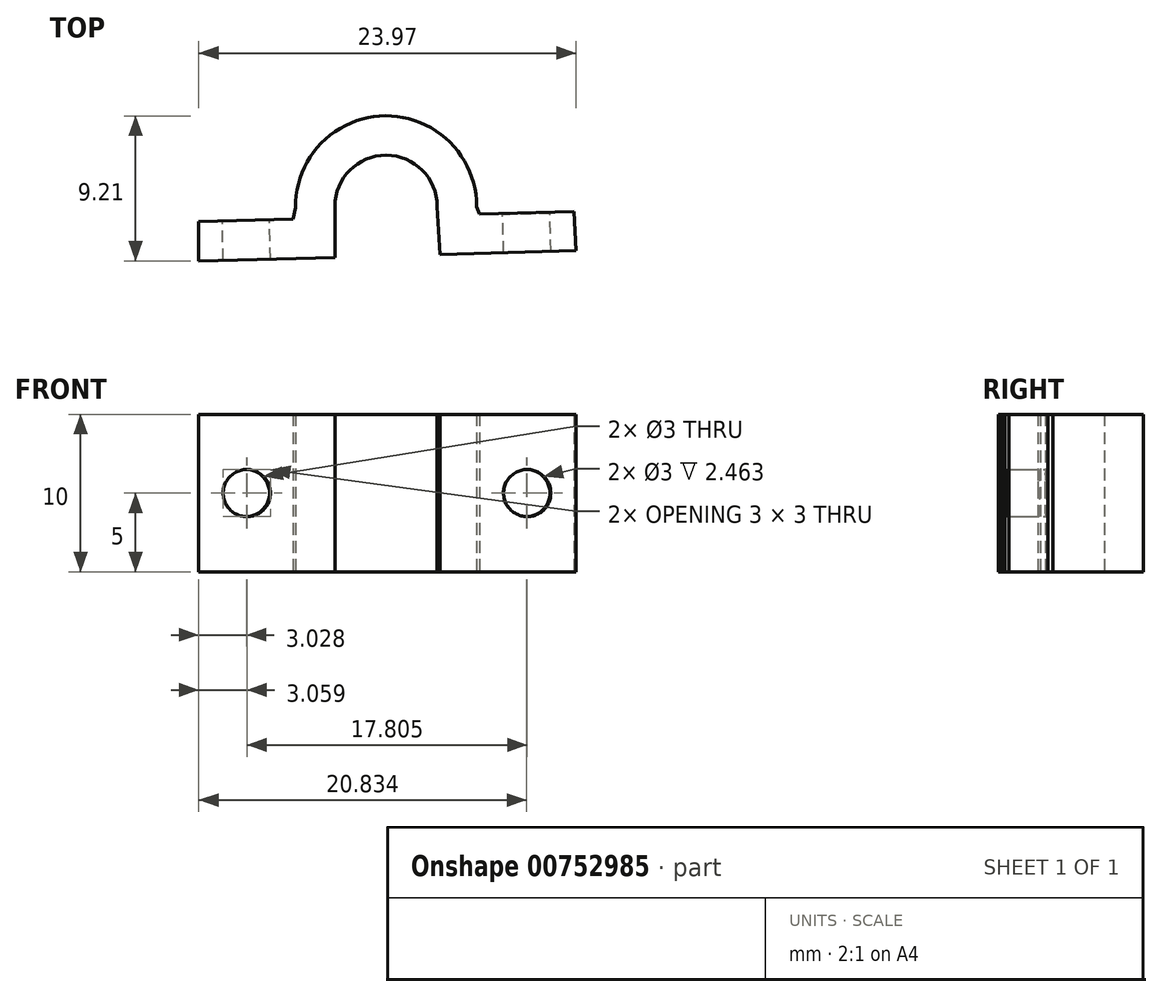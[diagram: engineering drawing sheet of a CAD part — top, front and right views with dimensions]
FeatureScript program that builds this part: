
annotation { "Feature Type Name" : "Feature", "Feature Type Description" : "" }
export const myFeature = defineFeature(function(context is Context, id is Id, definition is map)
    precondition{}
    {
        {
            var Q0;
            Q0=qCreatedBy(makeId("Top.planeOp"),FACE);
            var sketch = newSketch(context, id + "F0", { "sketchPlane" : qUnion([Q0])});
            skArc(sketch, "E0", {"start": v(3.25, 0) * mm, "mid": v(0, 3.25) * mm, "end": v(-3.25, 0) * mm});
            skPoint(sketch, "E1.orphan", {"position": v(0, -3.25) * mm});
            skLineSegment(sketch, "E2", {"start": v(-3.25, -3.25) * mm, "end": v(-11.9, -3.46) * mm});
            skLineSegment(sketch, "E3", {"start": v(-11.9, -3.46) * mm, "end": v(-11.9, -0.96) * mm});
            skLineSegment(sketch, "E4", {"start": v(-11.9, -0.96) * mm, "end": v(-5.9, -0.82) * mm});
            skLineSegment(sketch, "E5", {"start": v(0, 0) * mm, "end": v(-0.36, 13.25) * mm, "construction": true});
            skPoint(sketch, "E5.endSnap0", {"position": v(-0.36, 6.13) * mm});
            skLineSegment(sketch, "E6.MirrorCS", {"start": v(11.94, -0.32) * mm, "end": v(5.94, -0.5) * mm});
            skLineSegment(sketch, "E7.MirrorCS", {"start": v(12.07, -2.81) * mm, "end": v(11.94, -0.32) * mm});
            skLineSegment(sketch, "E8.MirrorCS", {"start": v(3.42, -3.07) * mm, "end": v(12.07, -2.81) * mm});
            skLineSegment(sketch, "E9", {"start": v(0, 3.25) * mm, "end": v(0, -3.25) * mm, "construction": true});
            skLineSegment(sketch, "E10", {"start": v(0, -3.25) * mm, "end": v(-3.25, -3.25) * mm, "construction": true});
            skLineSegment(sketch, "E11", {"start": v(-3.25, 0) * mm, "end": v(-3.25, -3.25) * mm});
            skLineSegment(sketch, "E12", {"start": v(3.25, 0) * mm, "end": v(3.42, -3.07) * mm});
            skArc(sketch, "E13.0", {"start": v(5.75, 0) * mm, "mid": v(-0.04, 5.75) * mm, "end": v(-5.75, -0.08) * mm});
            skLineSegment(sketch, "E14", {"start": v(-5.9, -0.82) * mm, "end": v(-5.75, -0.08) * mm});
            skLineSegment(sketch, "E15", {"start": v(5.94, -0.5) * mm, "end": v(5.75, 0) * mm});
            skSolve(sketch);
        }
        {
            var Q0;
            Q0 = qSketchRegion(id + "F0", true);
            extrude(context, id + "F1", {"entities" : qUnion([Q0]), "depth" : 10 * mm, "offsetDistance" : 25 * mm});
        }
        {
            var Q0;
            Q0=makeQuery(id+"F1.opExtrude","SWEPT_FACE",FACE,{"disambiguationData":[OSD([sQuery(id+"F0.wireOp",EDGE,"E4")])]});
            var sketch = newSketch(context, id + "F2", { "sketchPlane" : qUnion([Q0])});
            skLineSegment(sketch, "E16", {"start": v(11.92, 0) * mm, "end": v(11.92, 10) * mm, "construction": true});
            skCircle(sketch, "E17", {"center": v(8.92, 5) * mm, "radius": 1.5 * mm});
            skCircle(sketch, "E18.MirrorC", {"center": v(-8.89, 5) * mm, "radius": 1.5 * mm});
            skLineSegment(sketch, "E19.0", {"start": v(11.92, 0) * mm, "end": v(5.92, 0) * mm, "construction": true});
            skLineSegment(sketch, "E19.1", {"start": v(11.92, 10) * mm, "end": v(5.92, 10) * mm, "construction": true});
            skPoint(sketch, "E19.2", {"position": v(7.66, 0) * mm});
            skLineSegment(sketch, "E20", {"start": v(5.92, 0) * mm, "end": v(11.92, 10) * mm, "construction": true});
            skSolve(sketch);
        }
        {
            var Q0;
            Q0=sQuery(id+"F2.wireOp",VERTEX,"E17.center");
            var Q1;
            Q1=sQuery(id+"F2.wireOp",VERTEX,"E18.MirrorC.center");
            var Q2;
            Q2=makeQuery(id+"F1.opExtrude","SWEPT_BODY",BODY,{"disambiguationData":[OSD([sQuery(id+"F0.wireOp",EDGE,"E0"),sQuery(id+"F0.wireOp",EDGE,"vLbjqSUE-ySTp-fSFN-yZcK-jhC2w7Fs0Ytp"),sQuery(id+"F0.wireOp",EDGE,"r6u2Rahe-Nwup-FE6B-g2qP-wRSlcJ43wtVU"),sQuery(id+"F0.wireOp",EDGE,"5efc8ba7-78b5-4cee-a0f9-ba5f25261cf5.0"),sQuery(id+"F0.wireOp",EDGE,"5efc8ba7-78b5-4cee-a0f9-ba5f25261cf5.1"),sQuery(id+"F0.wireOp",EDGE,"5efc8ba7-78b5-4cee-a0f9-ba5f25261cf5.2"),sQuery(id+"F0.wireOp",EDGE,"IoEif2M4-6TRN-Kgu1-TaQc-xEdQMfZ22ch5"),sQuery(id+"F0.wireOp",EDGE,"E2"),sQuery(id+"F0.wireOp",EDGE,"E3"),sQuery(id+"F0.wireOp",EDGE,"E4"),sQuery(id+"F0.wireOp",EDGE,"E6.MirrorCS"),sQuery(id+"F0.wireOp",EDGE,"E7.MirrorCS"),sQuery(id+"F0.wireOp",EDGE,"E8.MirrorCS"),sQuery(id+"F0.wireOp",EDGE,"db6c8ddb-3f48-490e-8527-18ad76fe56bd3.MirrorCS")])]});
            hole(context, id + "F3", {"style" : HoleStyle.SIMPLE, "endStyle" : HoleEndStyle.THROUGH, "holeDiameter" : 3 * mm, "majorDiameter" : 5 * mm, "isTappedThrough" : true, "tappedDepth" : 12 * mm, "tapClearance" : 3, "startFromSketch" : true, "locations" : qUnion([Q0, Q1]), "scope" : qUnion([Q2])});
        }
    });
